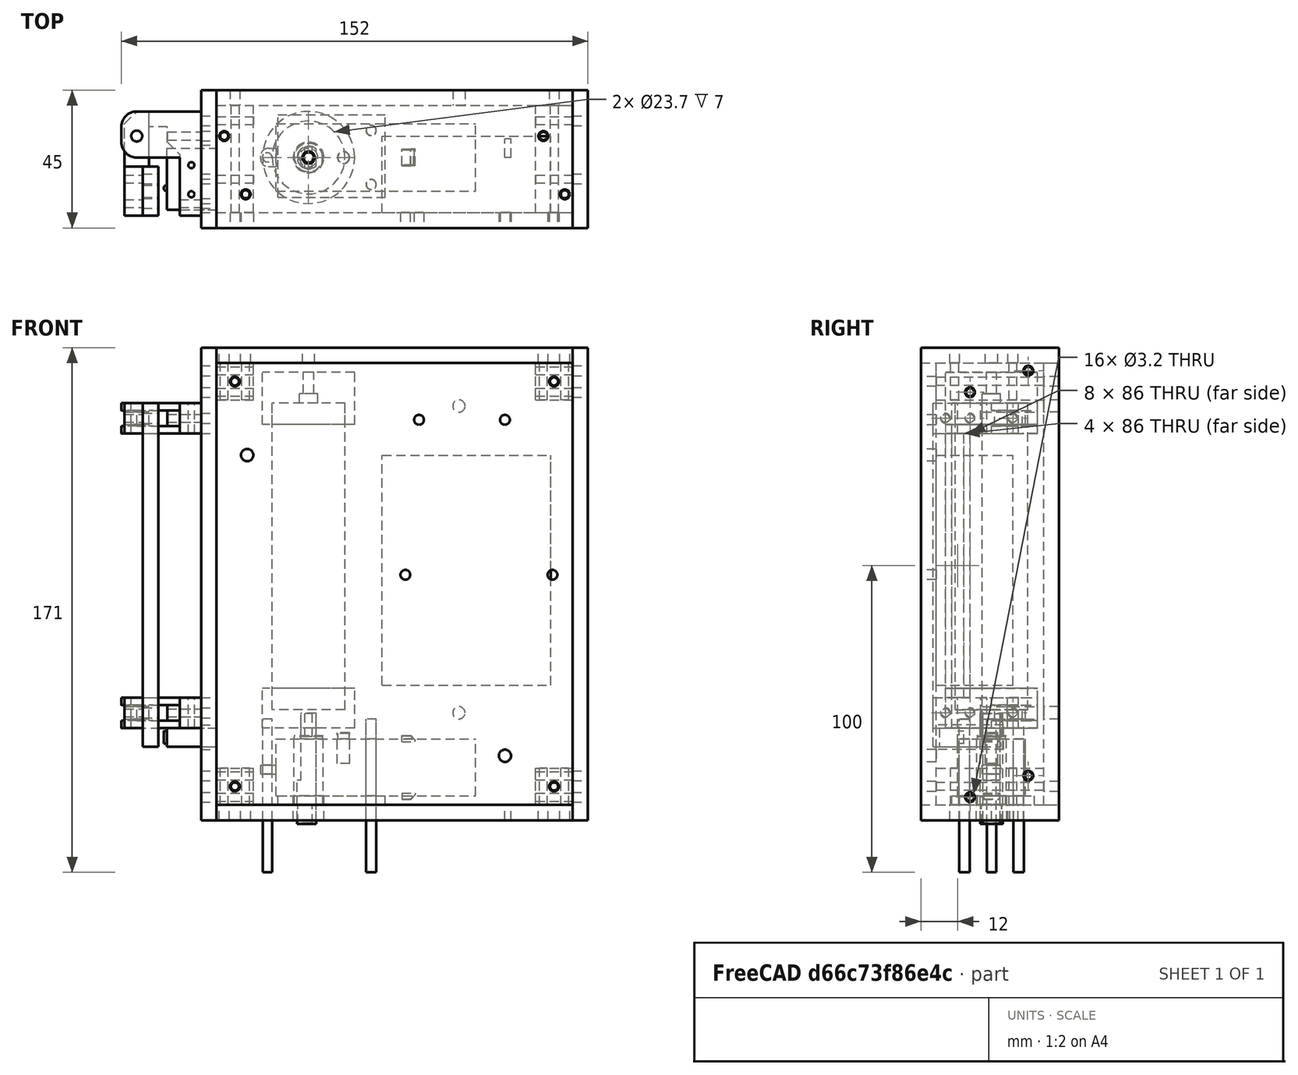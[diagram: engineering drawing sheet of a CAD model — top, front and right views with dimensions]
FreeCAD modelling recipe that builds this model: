
FCSTD DOCUMENT  (FreeCAD 0.16R6703 (Git))
Label: chicken-door-winder
License: All rights reserved
LicenseURL: http://en.wikipedia.org/wiki/All_rights_reserved
objects: Part::Cylinder×69, Part::Cut×59, Part::Fuse×59, Part::Box×34, Part::Chamfer×8, Part::Feature×7, App::DocumentObjectGroup×4, Part::Fillet×3, Part::Mirroring×2
note: 241 computed .brp shape members not serialized (recipe doc carries the construction recipe); baked Part::Feature solids carry a one-line shape summary decoded from their .brp

FEATURE [Part::Box] Box  label="Cube"
  Height = 18.5
  Length = 65
  Placement = pos=(0,-11,0) rot=(0,0,1;0rad)
  Width = 22
FEATURE [Part::Box] Box001  label="Cube001"
  Height = 3
  Length = 10
  Placement = pos=(-5,-3,7) rot=(0,0,1;0rad)
  Width = 6
FEATURE [Part::Cylinder] Cylinder
  Angle = 360
  Height = 10
  Placement = pos=(-2.8,0,3) rot=(0,0,1;0rad)
  Radius = 1.5
FEATURE [Part::Cut] Cut
  Base = -> Box001
  Tool = -> Cylinder
FEATURE [Part::Fillet] Fillet
  Base = -> Cut
  Edges = 1 edges r=2.5: [Edge1]
FEATURE [Part::Fillet] Fillet001
  Base = -> Fillet
  Edges = 1 edges r=2.5: [Edge3]
FEATURE [Part::Cylinder] Cylinder001  label="endhole"
  Angle = 360
  Height = 50
  Placement = pos=(-13.4,0,-22) rot=(0,0,1;0rad)
  Radius = 1.5
FEATURE [Part::Fuse] Fusion
  Base = -> Box
  Tool = -> Fillet001
FEATURE [Part::Cylinder] Cylinder002  label="Cylinder001"
  Angle = 360
  Height = 50
  Placement = pos=(31,8.8,-25) rot=(0,0,1;0rad)
  Radius = 1.7
FEATURE [Part::Cylinder] Cylinder003  label="Cylinder002"
  Angle = 360
  Height = 50
  Placement = pos=(31,-8.8,-25) rot=(0,0,1;0rad)
  Radius = 1.7
FEATURE [Part::Cylinder] Cylinder004  label="body-hole-1"
  Angle = 360
  Height = 50
  Placement = pos=(20.4,8.8,-22) rot=(0,0,1;0rad)
  Radius = 1.7
FEATURE [Part::Cylinder] Cylinder005  label="body-hole-2"
  Angle = 360
  Height = 50
  Placement = pos=(20.4,-8.8,-22) rot=(0,0,1;0rad)
  Radius = 1.7
FEATURE [Part::Cut] Cut001
  Base = -> Fusion
  Tool = -> Cylinder002
FEATURE [Part::Cut] Cut002
  Base = -> Cut001
  Tool = -> Cylinder003
FEATURE [Part::Cylinder] Cylinder006  label="Cylinder003"
  Angle = 360
  Height = 10
  Placement = pos=(22,0,10.2) rot=(0,0,1;0rad)
  Radius = 1.85
FEATURE [Part::Cylinder] Cylinder007  label="central-bump"
  Angle = 360
  Height = 10
  Placement = pos=(11.4,0,13.5) rot=(0,0,1;0rad)
  Radius = 2
FEATURE [Part::Fuse] Fusion001
  Base = -> Cut002
  Tool = -> Cylinder006
FEATURE [Part::Cylinder] Cylinder008  label="Cylinder004"
  Angle = 360
  Height = 22
  Placement = pos=(10.6,0,-2.8) rot=(0,0,1;0rad)
  Radius = 4.6
FEATURE [Part::Cylinder] Cylinder009  label="motor-boss"
  Angle = 360
  Height = 22.5
  Radius = 4.8
FEATURE [Part::Fuse] Fusion002
  Base = -> Fusion001
  Tool = -> Cylinder008
FEATURE [Part::Cylinder] Cylinder010  label="motor-boss001"
  Angle = 360
  Height = 35.7
  Placement = pos=(10.6,0,-9) rot=(0,0,1;0rad)
  Radius = 3.5
FEATURE [Part::Box] Box002  label="Cube002"
  Height = 40
  Length = 10
  Placement = pos=(11.75,-5,-11) rot=(0,0,1;0rad)
  Width = 10
FEATURE [Part::Box] Box003  label="Cube003"
  Height = 40
  Length = 10
  Placement = pos=(-0.55,-5,5) rot=(0,0,1;0rad)
  Width = 10
FEATURE [Part::Cut] Cut003
  Base = -> Cylinder010
  Tool = -> Box002
FEATURE [Part::Cut] Cut004
  Base = -> Cut003
  Tool = -> Box003
FEATURE [Part::Cylinder] Cylinder011  label="motor-boss002"
  Angle = 360
  Height = 36.1
  Placement = pos=(10.6,0,-9.2) rot=(0,0,1;0rad)
  Radius = 3.7
FEATURE [Part::Box] Box004  label="Cube004"
  Height = 40
  Length = 10
  Placement = pos=(13.05,-5,-11) rot=(0,0,1;0rad)
  Width = 10
FEATURE [Part::Box] Box005  label="Cube005"
  Height = 40
  Length = 10
  Placement = pos=(-1.85,-5,5) rot=(0,0,1;0rad)
  Width = 10
FEATURE [Part::Cut] Cut005
  Base = -> Cylinder011
  Tool = -> Box004
FEATURE [Part::Cut] Cut006  label="drive"
  Base = -> Cut005
  Placement = pos=(-10.6,0,3) rot=(0,0,1;0rad)
  Tool = -> Box005
FEATURE [Part::Fuse] Fusion003
  Base = -> Fusion002
  Tool = -> Cut004
FEATURE [Part::Box] Box006  label="Cube006"
  Height = 2
  Length = 4.3
  Placement = pos=(41,-2.5,17.53) rot=(0,0,1;0rad)
  Width = 5
FEATURE [Part::Chamfer] Chamfer
  Base = -> Box006
  Edges = 1 edges r=1.5: [Edge6]
FEATURE [Part::Box] Box007  label="Cube007"
  Height = 2
  Length = 4.3
  Placement = pos=(41,-2.5,17.53) rot=(0,0,1;0rad)
  Width = 5
FEATURE [Part::Chamfer] Chamfer001
  Base = -> Box007
  Edges = 1 edges r=1.5: [Edge6]
FEATURE [Part::Mirroring] Part__Mirroring  label="Chamfer001 (Mirror #1)"
  Base = (0,0,0)
  Normal = (0,0,1)
  Placement = pos=(0,0,18.4) rot=(0,0,1;0rad)
  Source = -> Chamfer001
FEATURE [Part::Fuse] Fusion004
  Base = -> Chamfer
  Tool = -> Part__Mirroring
FEATURE [Part::Box] Box008  label="Cube008"
  Height = 2
  Length = 4.4
  Placement = pos=(41,-2.7,17.63) rot=(0,0,1;0rad)
  Width = 5.4
FEATURE [Part::Chamfer] Chamfer002
  Base = -> Box008
  Edges = 1 edges r=1.5: [Edge6]
FEATURE [Part::Box] Box009  label="Cube009"
  Height = 2
  Length = 4.4
  Placement = pos=(41,-2.7,17.63) rot=(0,0,1;0rad)
  Width = 5.4
FEATURE [Part::Chamfer] Chamfer003
  Base = -> Box009
  Edges = 1 edges r=1.5: [Edge6]
FEATURE [Part::Mirroring] Part__Mirroring001  label="Chamfer001 (Mirror #1)001"
  Base = (0,0,0)
  Normal = (0,0,1)
  Placement = pos=(0,0,18.4) rot=(0,0,1;0rad)
  Source = -> Chamfer003
FEATURE [Part::Fuse] Fusion005  label="hook-bumps"
  Base = -> Chamfer002
  Placement = pos=(-10.6,0,3) rot=(0,0,1;0rad)
  Tool = -> Part__Mirroring001
FEATURE [App::DocumentObjectGroup] Group  label="Motor-holes"
  Group = -> [Cylinder001,Cylinder005,Cylinder004,Cylinder007,Cylinder009,Cut006,Fusion005]
FEATURE [Part::Fuse] Fusion006  label="Motor"
  Base = -> Fusion003
  Placement = pos=(-10.6,0,3) rot=(0,0,1;0rad)
  Tool = -> Fusion004
FEATURE [Part::Cylinder] Cylinder012  label="Cylinder005"
  Angle = 360
  Height = 13
  Placement = pos=(0,0,25) rot=(0,0,1;0rad)
  Radius = 15
FEATURE [Part::Cylinder] Cylinder013  label="Cylinder006"
  Angle = 360
  Height = 100
  Placement = pos=(0,0,31) rot=(0,0,1;0rad)
  Radius = 11.85
FEATURE [Part::Cylinder] Cylinder014  label="Cylinder007"
  Angle = 360
  Height = 17
  Placement = pos=(0,0,124) rot=(0,0,1;0rad)
  Radius = 15
FEATURE [Part::Box] Box010  label="arduino"
  Height = 75
  Length = 55
  Placement = pos=(24,-18,39) rot=(0,0,1;0rad)
  Width = 25
FEATURE [Part::Box] Box011  label="back-z"
  Height = 144
  Length = 116
  Placement = pos=(-30,-23,0) rot=(0,0,1;0rad)
  Width = 5
FEATURE [Part::Box] Box012  label="left-z"
  Height = 5
  Length = 116
  Placement = pos=(-30,-23,-5) rot=(0,0,1;0rad)
  Width = 45
FEATURE [Part::Box] Box013  label="right-z"
  Height = 5
  Length = 116
  Placement = pos=(-30,-23,144) rot=(0,0,1;0rad)
  Width = 45
FEATURE [Part::Box] Box014  label="bottom-z"
  Height = 154
  Length = 5
  Placement = pos=(-35,-23,-5) rot=(0,0,1;0rad)
  Width = 45
FEATURE [Part::Box] Box015  label="top-z"
  Height = 154
  Length = 5
  Placement = pos=(86,-23,-5) rot=(0,0,1;0rad)
  Width = 45
FEATURE [Part::Box] Box016  label="string-hole"
  Height = 86
  Length = 10
  Placement = pos=(-36,-15,35) rot=(0,0,1;0rad)
  Width = 8
FEATURE [Part::Cut] Cut007  label="bottom-y"
  Base = -> Box014
  Tool = -> Box016
FEATURE [Part::Box] Box017  label="corner-z"
  Height = 12
  Length = 12
  Placement = pos=(-30,-18,0) rot=(0,0,1;0rad)
  Width = 35
FEATURE [Part::Box] Box018  label="front-z"
  Height = 144
  Length = 116
  Placement = pos=(-30,17,0) rot=(0,0,1;0rad)
  Width = 5
FEATURE [Part::Cylinder] Cylinder015  label="Cylinder008"
  Angle = 360
  Height = 40
  Placement = pos=(-20.5,-12,-15) rot=(0,0,1;0rad)
  Radius = 1.6
FEATURE [Part::Cylinder] Cylinder016  label="Cylinder009"
  Angle = 360
  Height = 70
  Placement = pos=(-24,39,6) rot=(1,0,0;1.5708rad)
  Radius = 1.6
FEATURE [Part::Cylinder] Cylinder017  label="Cylinder010"
  Angle = 360
  Height = 40
  Placement = pos=(-27.5,7,-15) rot=(0,0,1;0rad)
  Radius = 1.6
FEATURE [Part::Cylinder] Cylinder018  label="Cylinder099"
  Angle = 360
  Height = 40
  Placement = pos=(-40,-7,2.5) rot=(0,1,0;1.5708rad)
  Radius = 1.6
FEATURE [Part::Cylinder] Cylinder019  label="Cylinder100"
  Angle = 360
  Height = 40
  Placement = pos=(-40,12,9.5) rot=(0,1,0;1.5708rad)
  Radius = 1.6
FEATURE [Part::Cylinder] Cylinder020  label="Cylinder101"
  Angle = 360
  Height = 40
  Placement = pos=(-20.5,-12,-15) rot=(0,0,1;0rad)
  Radius = 1.3
FEATURE [Part::Cylinder] Cylinder021  label="Cylinder102"
  Angle = 360
  Height = 40
  Placement = pos=(-27.5,7,-15) rot=(0,0,1;0rad)
  Radius = 1.3
FEATURE [Part::Cylinder] Cylinder022  label="Cylinder103"
  Angle = 360
  Height = 70
  Placement = pos=(-24,39,6) rot=(1,0,0;1.5708rad)
  Radius = 1.3
FEATURE [Part::Cylinder] Cylinder023  label="Cylinder104"
  Angle = 360
  Height = 40
  Placement = pos=(-40,-7,2.5) rot=(0,1,0;1.5708rad)
  Radius = 1.3
FEATURE [Part::Cylinder] Cylinder024  label="Cylinder105"
  Angle = 360
  Height = 40
  Placement = pos=(-40,12,9.5) rot=(0,1,0;1.5708rad)
  Radius = 1.3
FEATURE [Part::Fuse] Fusion007
  Base = -> Cylinder023
  Tool = -> Cylinder024
FEATURE [Part::Fuse] Fusion008
  Base = -> Cylinder022
  Tool = -> Fusion007
FEATURE [Part::Fuse] Fusion009
  Base = -> Cylinder021
  Tool = -> Fusion008
FEATURE [Part::Fuse] Fusion010  label="corner-block-holes"
  Base = -> Cylinder020
  Tool = -> Fusion009
FEATURE [Part::Fuse] Fusion011
  Base = -> Cylinder018
  Tool = -> Cylinder019
FEATURE [Part::Fuse] Fusion012
  Base = -> Cylinder017
  Tool = -> Fusion011
FEATURE [Part::Fuse] Fusion013
  Base = -> Cylinder016
  Tool = -> Fusion012
FEATURE [Part::Fuse] Fusion014  label="face-corner-holes"
  Base = -> Cylinder015
  Tool = -> Fusion013
FEATURE [Part::Cut] Cut008  label="corner-block"
  Base = -> Box017
  Tool = -> Fusion010
FEATURE [Part::Fuse] Fusion015  label="face-corner-holes001"
  Base = -> Cylinder015
  Placement = pos=(104,0,0) rot=(0,0,1;0rad)
  Tool = -> Fusion013
FEATURE [Part::Fuse] Fusion016  label="face-corner-holes002"
  Base = -> Cylinder015
  Placement = pos=(0,0,132) rot=(0,0,1;0rad)
  Tool = -> Fusion013
FEATURE [Part::Fuse] Fusion017  label="face-corner-holes003"
  Base = -> Cylinder015
  Placement = pos=(104,0,132) rot=(0,0,1;0rad)
  Tool = -> Fusion013
FEATURE [Part::Cut] Cut009  label="corner-block001"
  Base = -> Box017
  Placement = pos=(104,0,0) rot=(0,0,1;0rad)
  Tool = -> Fusion010
FEATURE [Part::Cut] Cut010  label="corner-block002"
  Base = -> Box017
  Placement = pos=(0,0,132) rot=(0,0,1;0rad)
  Tool = -> Fusion010
FEATURE [Part::Cut] Cut011  label="corner-block003"
  Base = -> Box017
  Placement = pos=(104,0,132) rot=(0,0,1;0rad)
  Tool = -> Fusion010
FEATURE [Part::Fuse] Fusion018  label="face-corner-holes004"
  Base = -> Cylinder015
  Tool = -> Fusion013
FEATURE [Part::Fuse] Fusion019  label="face-corner-holes005"
  Base = -> Cylinder015
  Tool = -> Fusion013
FEATURE [Part::Cut] Cut012  label="bottom-x"
  Base = -> Cut007
  Tool = -> Fusion014
FEATURE [Part::Cut] Cut013  label="back-y"
  Base = -> Box011
  Tool = -> Fusion018
FEATURE [Part::Cut] Cut014  label="left-y"
  Base = -> Box012
  Tool = -> Fusion019
FEATURE [Part::Fuse] Fusion020  label="face-corner-holes006"
  Base = -> Cylinder015
  Tool = -> Fusion013
FEATURE [Part::Cut] Cut015  label="front-y"
  Base = -> Box018
  Tool = -> Fusion020
FEATURE [Part::Fuse] Fusion021  label="face-corner-holes007"
  Base = -> Cylinder015
  Placement = pos=(104,0,0) rot=(0,0,1;0rad)
  Tool = -> Fusion013
FEATURE [Part::Fuse] Fusion022  label="face-corner-holes008"
  Base = -> Cylinder015
  Placement = pos=(104,0,0) rot=(0,0,1;0rad)
  Tool = -> Fusion013
FEATURE [Part::Fuse] Fusion023  label="face-corner-holes009"
  Base = -> Cylinder015
  Placement = pos=(104,0,0) rot=(0,0,1;0rad)
  Tool = -> Fusion013
FEATURE [Part::Cut] Cut016  label="top-y"
  Base = -> Box015
  Tool = -> Fusion015
FEATURE [Part::Cut] Cut017  label="back-x"
  Base = -> Cut013
  Tool = -> Fusion021
FEATURE [Part::Cut] Cut018  label="left-x"
  Base = -> Cut014
  Tool = -> Fusion022
FEATURE [Part::Cut] Cut019  label="front-x"
  Base = -> Cut015
  Tool = -> Fusion023
FEATURE [Part::Fuse] Fusion024  label="face-corner-holes010"
  Base = -> Cylinder015
  Placement = pos=(0,0,132) rot=(0,0,1;0rad)
  Tool = -> Fusion013
FEATURE [Part::Fuse] Fusion025  label="face-corner-holes011"
  Base = -> Cylinder015
  Placement = pos=(0,0,132) rot=(0,0,1;0rad)
  Tool = -> Fusion013
FEATURE [Part::Fuse] Fusion026  label="face-corner-holes012"
  Base = -> Cylinder015
  Placement = pos=(0,0,132) rot=(0,0,1;0rad)
  Tool = -> Fusion013
FEATURE [Part::Cut] Cut020  label="right-y"
  Base = -> Box013
  Tool = -> Fusion016
FEATURE [Part::Cut] Cut021  label="bottom-w"
  Base = -> Cut012
  Tool = -> Fusion024
FEATURE [Part::Cut] Cut022  label="back-w"
  Base = -> Cut017
  Tool = -> Fusion025
FEATURE [Part::Cut] Cut023  label="front-w"
  Base = -> Cut019
  Tool = -> Fusion026
FEATURE [Part::Fuse] Fusion027  label="face-corner-holes013"
  Base = -> Cylinder015
  Placement = pos=(104,0,132) rot=(0,0,1;0rad)
  Tool = -> Fusion013
FEATURE [Part::Fuse] Fusion028  label="face-corner-holes014"
  Base = -> Cylinder015
  Placement = pos=(104,0,132) rot=(0,0,1;0rad)
  Tool = -> Fusion013
FEATURE [Part::Fuse] Fusion029  label="face-corner-holes015"
  Base = -> Cylinder015
  Placement = pos=(104,0,132) rot=(0,0,1;0rad)
  Tool = -> Fusion013
FEATURE [Part::Cut] Cut024  label="top-x"
  Base = -> Cut016
  Tool = -> Fusion027
FEATURE [Part::Cut] Cut025  label="right-x"
  Base = -> Cut020
  Tool = -> Fusion028
FEATURE [Part::Cut] Cut026  label="front-v"
  Base = -> Cut023
  Tool = -> Fusion017
FEATURE [Part::Cut] Cut027  label="back-v"
  Base = -> Cut022
  Tool = -> Fusion029
FEATURE [Part::Cylinder] Cylinder025  label="Cylinder032"
  Angle = 360
  Height = 50
  Placement = pos=(74.5,7,54) rot=(1,0,0;1.5708rad)
  Radius = 1.6
FEATURE [Part::Cylinder] Cylinder026  label="Cylinder033"
  Angle = 360
  Height = 50
  Placement = pos=(26.54,7,54) rot=(1,0,0;1.5708rad)
  Radius = 1.6
FEATURE [Part::Cylinder] Cylinder027  label="Cylinder034"
  Angle = 360
  Height = 50
  Placement = pos=(59,7,104.5) rot=(1,0,0;1.5708rad)
  Radius = 1.6
FEATURE [Part::Cylinder] Cylinder028  label="Cylinder035"
  Angle = 360
  Height = 50
  Placement = pos=(31,7,104.5) rot=(1,0,0;1.5708rad)
  Radius = 1.6
FEATURE [Part::Fuse] Fusion031
  Base = -> Cylinder025
  Tool = -> Cylinder026
FEATURE [Part::Fuse] Fusion032
  Base = -> Cylinder028
  Tool = -> Fusion031
FEATURE [Part::Fuse] Fusion033  label="arduino-holes"
  Base = -> Cylinder027
  Placement = pos=(5,0,21) rot=(0,0,1;0rad)
  Tool = -> Fusion032
FEATURE [Part::Cut] Cut028  label="back-u"
  Base = -> Cut027
  Tool = -> Fusion033
FEATURE [Part::Cylinder] Cylinder029  label="motor-boss003"
  Angle = 360
  Height = 22.5
  Placement = pos=(0,0,-12) rot=(0,0,1;0rad)
  Radius = 5
FEATURE [Part::Cylinder] Cylinder030  label="body-hole-003"
  Angle = 360
  Height = 50
  Placement = pos=(20.4,8.8,-22) rot=(0,0,1;0rad)
  Radius = 1.6
FEATURE [Part::Cylinder] Cylinder031  label="body-hole-004"
  Angle = 360
  Height = 50
  Placement = pos=(20.4,-8.8,-22) rot=(0,0,1;0rad)
  Radius = 1.6
FEATURE [Part::Fuse] Fusion034
  Base = -> Cylinder029
  Tool = -> Cylinder030
FEATURE [Part::Fuse] Fusion035  label="motor-holes-z"
  Base = -> Cylinder031
  Tool = -> Fusion034
FEATURE [Part::Fuse] Fusion036  label="motor-holes-y"
  Base = -> Cylinder031
  Tool = -> Fusion034
FEATURE [Part::Cut] Cut029  label="left-w"
  Base = -> Cut018
  Tool = -> Fusion035
FEATURE [Part::Box] Box019  label="motor-spacer-a"
  Height = 3
  Length = 35
  Placement = pos=(-10,-13,0) rot=(0,0,1;0rad)
  Width = 27
FEATURE [Part::Cut] Cut030  label="motor-spacer"
  Base = -> Box019
  Tool = -> Fusion036
FEATURE [Part::Box] Box020  label="string-switch-a"
  Height = 112
  Length = 5
  Placement = pos=(-43,-19,19) rot=(0,0,1;0rad)
  Width = 16
FEATURE [Part::Box] Box021  label="string-hole001"
  Height = 86
  Length = 10
  Placement = pos=(-46,-13,35) rot=(0,0,1;0rad)
  Width = 4
FEATURE [Part::Cut] Cut031  label="string-slot-b"
  Base = -> Box020
  Placement = pos=(-11,0,0) rot=(0,0,1;0rad)
  Tool = -> Box021
FEATURE [Part::Box] Box024  label="Cube012"
  Height = 4
  Length = 8
  Placement = pos=(-60,-19,28) rot=(0,0,1;0rad)
  Width = 34
FEATURE [Part::Cylinder] Cylinder058  label="Cylinder336"
  Angle = 360
  Height = 23
  Placement = pos=(-11,18,-5) rot=(-0.57735,0.57735,0.57735;2.0944rad)
  Radius = 1.4
FEATURE [Part::Fuse] Fusion037
  Tool = -> Cylinder058
FEATURE [Part::Cylinder] Cylinder059  label="Cylinder337"
  Angle = 360
  Height = 15
  Placement = pos=(8,5,14.5) rot=(1,0,0;1.5708rad)
  Radius = 1
FEATURE [Part::Fuse] Fusion038  label="185 microswitch002"
  Base = -> Cylinder059
  Placement = pos=(-46.2,-17,25) rot=(-1,0,0;1.5708rad)
  Tool = -> Fusion037
FEATURE [Part::Box] Box026  label="Cube014"
  Height = 10
  Length = 6
  Placement = pos=(-60,-19,25) rot=(0,0,1;0rad)
  Width = 16
FEATURE [Part::Box] Box027  label="Cube015"
  Height = 10
  Length = 4
  Placement = pos=(-54,-19,25) rot=(0,0,1;0rad)
  Width = 16
FEATURE [Part::Cut] Cut033
  Base = -> Box024
  Tool = -> Box027
FEATURE [Part::Fuse] Fusion039  label="switch-rocker-a"
  Base = -> Box026
  Tool = -> Cut033
FEATURE [Part::Box] Box028  label="Cube016"
  Height = 8
  Length = 10
  Placement = pos=(-37,-18,18) rot=(0,0,1;0rad)
  Width = 22
FEATURE [Part::Cut] Cut034  label="bottom-v"
  Base = -> Cut021
  Tool = -> Box028
FEATURE [Part::Cylinder] Cylinder060  label="Cylinder338"
  Angle = 360
  Height = 40
  Placement = pos=(-56,7,15) rot=(0,0,1;0rad)
  Radius = 1.8
FEATURE [Part::Cut] Cut035  label="switch-rocker-b"
  Base = -> Fusion039
  Placement = pos=(0,0,96) rot=(0,0,1;0rad)
  Tool = -> Cylinder060
FEATURE [Part::Cylinder] Cylinder064  label="Cylinder342"
  Angle = 360
  Height = 40
  Placement = pos=(-87,-7,30) rot=(0,1,0;1.5708rad)
  Radius = 1.6
FEATURE [Part::Cylinder] Cylinder065  label="Cylinder343"
  Angle = 360
  Height = 40
  Placement = pos=(-67,-15,30) rot=(0,1,0;1.5708rad)
  Radius = 1.6
FEATURE [Part::Fuse] Fusion042  label="rocker-screw-holes-b"
  Base = -> Cylinder064
  Placement = pos=(0,0,96) rot=(0,0,1;0rad)
  Tool = -> Cylinder065
FEATURE [Part::Box] Box029  label="Cube017"
  Height = 10
  Length = 26
  Placement = pos=(-50,0,26) rot=(0,0,1;0rad)
  Width = 15
FEATURE [Part::Box] Box030  label="Cube018"
  Height = 5
  Length = 15
  Placement = pos=(-50,-2,28.5) rot=(0,0,1;0rad)
  Width = 19
FEATURE [Part::Box] Box031  label="Cube019"
  Height = 4
  Length = 8
  Placement = pos=(-60,-19,28) rot=(0,0,1;0rad)
  Width = 34
FEATURE [Part::Cut] Cut037
  Base = -> Box029
  Placement = pos=(-11,0,-1) rot=(0,0,1;0rad)
  Tool = -> Box030
FEATURE [Part::Box] Box032  label="Cube020"
  Height = 10
  Length = 7
  Placement = pos=(-42,-19,25) rot=(0,0,1;0rad)
  Width = 20
FEATURE [Part::Box] Box033  label="Cube021"
  Height = 10
  Length = 6
  Placement = pos=(-60,-19,25) rot=(0,0,1;0rad)
  Width = 16
FEATURE [Part::Box] Box034  label="Cube022"
  Height = 10
  Length = 4
  Placement = pos=(-54,-19,25) rot=(0,0,1;0rad)
  Width = 16
FEATURE [Part::Cut] Cut038
  Base = -> Box031
  Tool = -> Box034
FEATURE [Part::Fuse] Fusion044  label="switch-rocker-a001"
  Base = -> Box033
  Tool = -> Cut038
FEATURE [Part::Chamfer] Chamfer006
  Base = -> Cut037
  Edges = 1 edges r=5: [Edge18]
FEATURE [Part::Chamfer] Chamfer007
  Base = -> Chamfer006
  Edges = 1 edges r=5: [Edge9]
FEATURE [Part::Fuse] Fusion045  label="switch-hinge-a001"
  Base = -> Box032
  Tool = -> Chamfer007
FEATURE [Part::Cylinder] Cylinder067  label="Cylinder345"
  Angle = 360
  Height = 40
  Placement = pos=(-56,7,15) rot=(0,0,1;0rad)
  Radius = 1.8
FEATURE [Part::Cylinder] Cylinder068  label="Cylinder346"
  Angle = 360
  Height = 40
  Placement = pos=(-92,-7,30) rot=(0,1,0;1.5708rad)
  Radius = 1.3
FEATURE [Part::Cylinder] Cylinder069  label="Cylinder347"
  Angle = 360
  Height = 40
  Placement = pos=(-56,7,15) rot=(0,0,1;0rad)
  Radius = 1.8
FEATURE [Part::Cut] Cut039  label="switch-rocker-b001"
  Base = -> Fusion044
  Tool = -> Cylinder067
FEATURE [Part::Cut] Cut040  label="switch-hinge-b001"
  Base = -> Fusion045
  Tool = -> Cylinder069
FEATURE [Part::Cylinder] Cylinder070  label="Cylinder348"
  Angle = 360
  Height = 40
  Placement = pos=(-67,-15,30) rot=(0,1,0;1.5708rad)
  Radius = 1.3
FEATURE [Part::Fuse] Fusion046  label="rocker-screw-holes-a001"
  Base = -> Cylinder068
  Tool = -> Cylinder070
FEATURE [Part::Cylinder] Cylinder071  label="Cylinder349"
  Angle = 360
  Height = 40
  Placement = pos=(-87,-7,30) rot=(0,1,0;1.5708rad)
  Radius = 1.6
FEATURE [Part::Cylinder] Cylinder072  label="Cylinder350"
  Angle = 360
  Height = 40
  Placement = pos=(-67,-15,30) rot=(0,1,0;1.5708rad)
  Radius = 1.6
FEATURE [Part::Fuse] Fusion047  label="rocker-screw-holes-b001"
  Base = -> Cylinder071
  Tool = -> Cylinder072
FEATURE [Part::Cylinder] Cylinder073  label="Cylinder351"
  Angle = 360
  Height = 40
  Placement = pos=(-48,7,30) rot=(0,1,0;1.5708rad)
  Radius = 1.3
FEATURE [Part::Fuse] Fusion048  label="hinge-screw-holes-b001"
  Base = -> Fusion046
  Tool = -> Cylinder073
FEATURE [Part::Cylinder] Cylinder074  label="Cylinder352"
  Angle = 360
  Height = 40
  Placement = pos=(-67,7,30) rot=(0,1,0;1.5708rad)
  Radius = 1.6
FEATURE [Part::Cylinder] Cylinder075  label="Cylinder353"
  Angle = 360
  Height = 40
  Placement = pos=(-67,7,126) rot=(0,1,0;1.5708rad)
  Radius = 1.6
FEATURE [Part::Fuse] Fusion049  label="rocker-screw-holes-c"
  Base = -> Fusion047
  Tool = -> Cylinder074
FEATURE [Part::Fuse] Fusion050  label="rocker-screw-holes-d"
  Base = -> Fusion042
  Tool = -> Cylinder075
FEATURE [Part::Cylinder] Cylinder076  label="Cylinder354"
  Angle = 360
  Height = 40
  Placement = pos=(-87,-7,30) rot=(0,1,0;1.5708rad)
  Radius = 1.6
FEATURE [Part::Cylinder] Cylinder077  label="Cylinder355"
  Angle = 360
  Height = 40
  Placement = pos=(-67,-15,30) rot=(0,1,0;1.5708rad)
  Radius = 1.6
FEATURE [Part::Fuse] Fusion051  label="rocker-screw-holes-b002"
  Base = -> Cylinder076
  Placement = pos=(0,0,96) rot=(0,0,1;0rad)
  Tool = -> Cylinder077
FEATURE [Part::Cylinder] Cylinder078  label="Cylinder356"
  Angle = 360
  Height = 40
  Placement = pos=(-87,-7,30) rot=(0,1,0;1.5708rad)
  Radius = 1.6
FEATURE [Part::Cylinder] Cylinder079  label="Cylinder357"
  Angle = 360
  Height = 40
  Placement = pos=(-67,-15,30) rot=(0,1,0;1.5708rad)
  Radius = 1.6
FEATURE [Part::Fuse] Fusion052  label="rocker-screw-holes-b003"
  Base = -> Cylinder078
  Tool = -> Cylinder079
FEATURE [Part::Cylinder] Cylinder080  label="Cylinder358"
  Angle = 360
  Height = 40
  Placement = pos=(-67,7,30) rot=(0,1,0;1.5708rad)
  Radius = 1.6
FEATURE [Part::Cylinder] Cylinder081  label="Cylinder359"
  Angle = 360
  Height = 40
  Placement = pos=(-67,7,126) rot=(0,1,0;1.5708rad)
  Radius = 1.6
FEATURE [Part::Fuse] Fusion053  label="rocker-screw-holes-c001"
  Base = -> Fusion052
  Tool = -> Cylinder080
FEATURE [Part::Fuse] Fusion054  label="rocker-screw-holes-d001"
  Base = -> Fusion051
  Tool = -> Cylinder081
FEATURE [Part::Cut] Cut041
  Base = -> Cut031
  Tool = -> Fusion049
FEATURE [Part::Cut] Cut042  label="string-slot-c"
  Base = -> Cut041
  Tool = -> Fusion050
FEATURE [Part::Cut] Cut043
  Base = -> Cut034
  Tool = -> Fusion053
FEATURE [Part::Cut] Cut044  label="bottom-a"
  Base = -> Cut043
  Tool = -> Fusion054
FEATURE [Part::Cylinder] Cylinder082  label="Cylinder360"
  Angle = 360
  Height = 40
  Placement = pos=(-92,-7,30) rot=(0,1,0;1.5708rad)
  Radius = 1.3
FEATURE [Part::Cylinder] Cylinder083  label="Cylinder361"
  Angle = 360
  Height = 40
  Placement = pos=(-67,-15,30) rot=(0,1,0;1.5708rad)
  Radius = 1.3
FEATURE [Part::Fuse] Fusion055  label="rocker-screw-holes-a002"
  Base = -> Cylinder082
  Tool = -> Cylinder083
FEATURE [Part::Cylinder] Cylinder084  label="Cylinder362"
  Angle = 360
  Height = 40
  Placement = pos=(-48,7,30) rot=(0,1,0;1.5708rad)
  Radius = 1.3
FEATURE [Part::Fuse] Fusion056  label="hinge-screw-holes-b002"
  Base = -> Fusion055
  Placement = pos=(0,0,96) rot=(0,0,1;0rad)
  Tool = -> Cylinder084
FEATURE [Part::Cylinder] Cylinder085  label="Cylinder363"
  Angle = 360
  Height = 40
  Placement = pos=(-92,-7,30) rot=(0,1,0;1.5708rad)
  Radius = 1.3
FEATURE [Part::Cylinder] Cylinder086  label="Cylinder364"
  Angle = 360
  Height = 40
  Placement = pos=(-67,-15,30) rot=(0,1,0;1.5708rad)
  Radius = 1.3
FEATURE [Part::Fuse] Fusion057  label="rocker-screw-holes-a003"
  Base = -> Cylinder085
  Tool = -> Cylinder086
FEATURE [Part::Cylinder] Cylinder087  label="Cylinder365"
  Angle = 360
  Height = 40
  Placement = pos=(-48,7,30) rot=(0,1,0;1.5708rad)
  Radius = 1.3
FEATURE [Part::Fuse] Fusion058  label="hinge-screw-holes-b003"
  Base = -> Fusion057
  Tool = -> Cylinder087
FEATURE [Part::Cut] Cut046  label="switch-hinge-d"
  Base = -> Cut040
  Tool = -> Fusion048
FEATURE [Part::Cut] Cut047  label="switch-rocker-c"
  Base = -> Cut039
  Tool = -> Fusion058
FEATURE [Part::Cut] Cut048  label="switch-rocker-d"
  Base = -> Cut035
  Tool = -> Fusion056
FEATURE [Part::Fillet] Fillet003  label="switch-hinge-f"
  Base = -> Cut046
  Edges = 4 edges r=5: [Edge29,Edge40,Edge60,Edge64]
FEATURE [Part::Chamfer] Chamfer008  label="switch-rocker-f"
  Base = -> Cut047
  Edges = 1 edges r=4: [Edge33]
FEATURE [Part::Chamfer] Chamfer009  label="switch-rocker-g"
  Base = -> Cut048
  Edges = 1 edges r=4: [Edge33]
FEATURE [Part::Cylinder] Cylinder088  label="Cylinder366"
  Angle = 360
  Height = 23
  Placement = pos=(-11,18,-5) rot=(-0.57735,0.57735,0.57735;2.0944rad)
  Radius = 1.4
FEATURE [Part::Fuse] Fusion059
  Tool = -> Cylinder088
FEATURE [Part::Cylinder] Cylinder089  label="Cylinder367"
  Angle = 360
  Height = 15
  Placement = pos=(8,5,14.5) rot=(1,0,0;1.5708rad)
  Radius = 1
FEATURE [Part::Fuse] Fusion060  label="185 microswitch003"
  Base = -> Cylinder089
  Placement = pos=(-46.2,-17,25) rot=(-1,0,0;1.5708rad)
  Tool = -> Fusion059
FEATURE [Part::Cut] Cut049  label="switch-hinge-i"
  Base = -> Fillet003
  Tool = -> Fusion060
FEATURE [Part::Box] Box035  label="Cube023"
  Height = 8
  Length = 14
  Placement = pos=(-52,10,26) rot=(0,0,1;0rad)
  Width = 5
FEATURE [Part::Fuse] Fusion061  label="switch-hinge-j"
  Base = -> Cut049
  Tool = -> Box035
FEATURE [Part::Fuse] Fusion062  label="switch-hinge-k"
  Base = -> Cut049
  Placement = pos=(0,0,96) rot=(0,0,1;0rad)
  Tool = -> Box035
FEATURE [Part::Cylinder] Cylinder090  label="Cylinder368"
  Angle = 360
  Height = 30
  Placement = pos=(0,0,128) rot=(0,0,1;0rad)
  Radius = 1.7
FEATURE [Part::Cylinder] Cylinder091  label="Cylinder369"
  Angle = 360
  Height = 10
  Placement = pos=(0,0,124) rot=(0,0,1;0rad)
  Radius = 3
FEATURE [Part::Cylinder] Cylinder092  label="Cylinder370"
  Angle = 360
  Height = 100
  Placement = pos=(0,0,31) rot=(0,0,1;0rad)
  Radius = 11.85
FEATURE [Part::Cut] Cut050  label="winder-end-a"
  Base = -> Cylinder014
  Tool = -> Cylinder092
FEATURE [Part::Cylinder] Cylinder093  label="Cylinder371"
  Angle = 360
  Height = 30
  Placement = pos=(0,0,128) rot=(0,0,1;0rad)
  Radius = 2
FEATURE [Part::Cut] Cut051
  Base = -> Cut050
  Tool = -> Cylinder090
FEATURE [Part::Cut] Cut052  label="winder-end-free"
  Base = -> Cut051
  Tool = -> Cylinder091
FEATURE [Part::Cut] Cut053  label="right-a"
  Base = -> Cut025
  Tool = -> Cylinder093
FEATURE [Part::Cylinder] Cylinder094  label="winder"
  Angle = 360
  Height = 100
  Placement = pos=(0,0,31) rot=(0,0,1;0rad)
  Radius = 11.85
FEATURE [Part::Cut] Cut054
  Base = -> Cylinder012
  Tool = -> Cylinder013
FEATURE [Part::Cut] Cut055  label="drive001"
  Base = -> Cut005
  Placement = pos=(-10.6,0,3) rot=(0,0,1;0rad)
  Tool = -> Box005
FEATURE [Part::Cut] Cut056  label="winder-end-motor"
  Base = -> Cut054
  Tool = -> Cut055
FEATURE [App::DocumentObjectGroup] Group003  label="Printed"
  Group = -> [Cut008,Cut009,Cut010,Cut011,Cut030,Chamfer008,Chamfer009,Fusion061,Fusion062,Cut052,Cut056]
FEATURE [Part::Cylinder] Cylinder095  label="Cylinder372"
  Angle = 360
  Height = 10
  Placement = pos=(49,25,30) rot=(1,0,0;1.5708rad)
  Radius = 2
FEATURE [Part::Cylinder] Cylinder096  label="Cylinder373"
  Angle = 360
  Height = 10
  Placement = pos=(-20,-15,114) rot=(1,0,0;1.5708rad)
  Radius = 2
FEATURE [Part::Cylinder] Cylinder097  label="Cylinder374"
  Angle = 360
  Height = 10
  Placement = pos=(64,-15,16) rot=(1,0,0;1.5708rad)
  Radius = 2
FEATURE [Part::Cylinder] Cylinder098  label="Cylinder375"
  Angle = 360
  Height = 10
  Placement = pos=(49,25,130) rot=(1,0,0;1.5708rad)
  Radius = 2
FEATURE [Part::Cut] Cut057
  Base = -> Cut028
  Tool = -> Cylinder097
FEATURE [Part::Cut] Cut058  label="back-a"
  Base = -> Cut057
  Tool = -> Cylinder096
FEATURE [Part::Cut] Cut059
  Base = -> Cut026
  Tool = -> Cylinder098
FEATURE [Part::Cut] Cut060  label="front-a"
  Base = -> Cut059
  Tool = -> Cylinder095
FEATURE [Part::Box] Box036  label="Cube024"
  Height = 10
  Length = 2
  Placement = pos=(64,0,-8) rot=(0,0,1;0rad)
  Width = 6
FEATURE [Part::Cut] Cut061  label="left-a"
  Base = -> Cut029
  Tool = -> Box036
FEATURE [App::DocumentObjectGroup] Group002  label="Laser-cut"
  Group = -> [Cut024,Cut042,Cut044,Cut053,Cut058,Cut060,Cut061]
FEATURE [Part::Feature] Cut024_cs  label="xs-top"
  Placement = pos=(0,0,88.5) rot=(0,1,0;1.5708rad)
  shape: bbox 154 x 45 x 2e-07 mm, 0 faces, 0 solids (baked)
FEATURE [Part::Feature] Cut042_cs  label="xs-string-slot"
  Placement = pos=(0,0,0) rot=(0,1,0;1.5708rad)
  shape: bbox 112 x 16 x 2e-07 mm, 0 faces, 0 solids (baked)
FEATURE [Part::Feature] Cut044_cs  label="xs-bottom"
  Placement = pos=(0,0,0) rot=(0,1,0;1.5708rad)
  shape: bbox 154 x 45 x 2e-07 mm, 0 faces, 0 solids (baked)
FEATURE [Part::Feature] Cut053_cs  label="xs-right"
  shape: bbox 116 x 45 x 2e-07 mm, 0 faces, 0 solids (baked)
FEATURE [Part::Feature] Cut060_cs  label="xs-front"
  Placement = pos=(0,0,0) rot=(1,0,0;1.5708rad)
  shape: bbox 116 x 144 x 2e-07 mm, 0 faces, 0 solids (baked)
FEATURE [Part::Feature] Cut061_cs  label="xs-left"
  shape: bbox 116 x 45 x 2e-07 mm, 0 faces, 0 solids (baked)
FEATURE [Part::Feature] Cut058_cs  label="xs-back"
  shape: bbox 116 x 144 x 2e-07 mm, 0 faces, 0 solids (baked)
FEATURE [App::DocumentObjectGroup] Group004  label="laser-sections"
  Group = -> [Cut024_cs,Cut042_cs,Cut044_cs,Cut053_cs,Cut060_cs,Cut061_cs,Cut058_cs]
